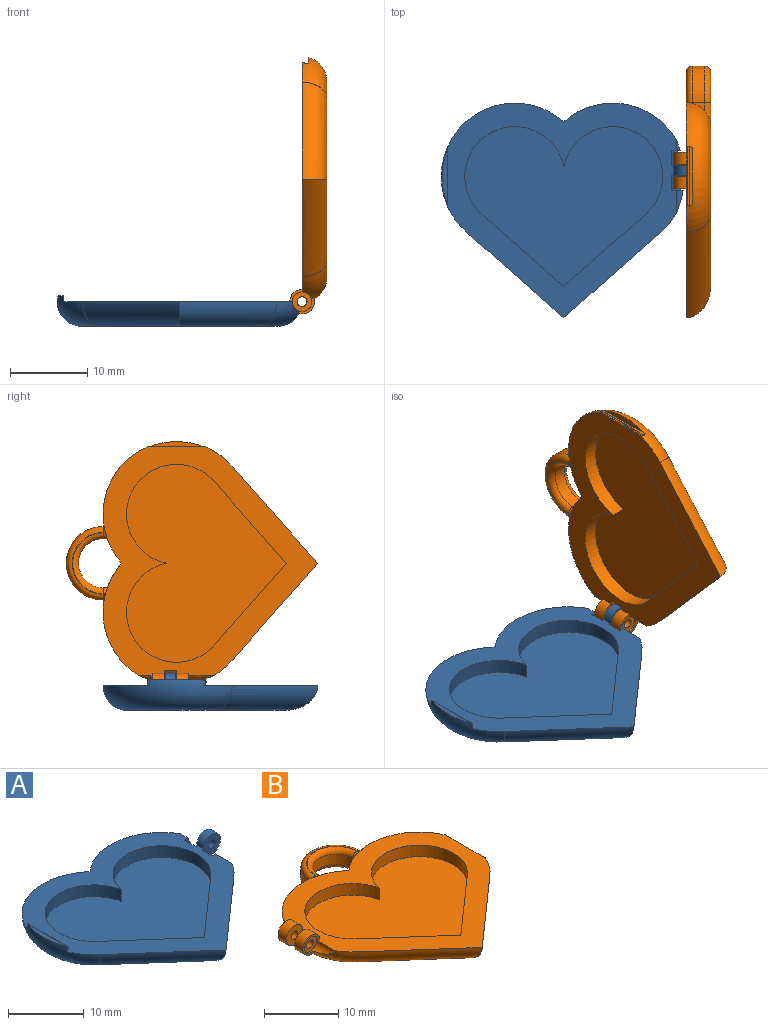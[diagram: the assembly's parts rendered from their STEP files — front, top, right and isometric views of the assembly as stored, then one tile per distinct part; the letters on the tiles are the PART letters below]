
ASSEMBLY  parts=2 mates=1
PART A: 31 faces, bbox 34.1x28.6x5.4 mm
  f0: torus R=6.35mm, axis (0,0,1), area 124.9mm2, adj f1,f2,f6,f7,f9,f20,f21,f22
  f1: cylinder r=1.27mm len=3.03mm, axis (0,1,0), area 2.4mm2, adj f0,f2,f27
  f2: plane 29.67x27.83mm, normal (0,0,1), area 243mm2, adj f0,f1,f4,f5,f6,f7,f8,f11
  f3: cylinder r=0.64mm len=1.27mm, axis (0,-1,0), area 5.1mm2, adj f22,f25
  f4: cylinder r=3.17mm len=14.69mm, axis (0.75,0.66,0), area 76.6mm2, adj f2,f5,f7,f9
  f5: cylinder r=3.17mm len=14.69mm, axis (0.75,-0.66,0), area 76.6mm2, adj f2,f4,f8,f9
  f6: torus R=6.35mm, axis (0,0,1), area 144.4mm2, adj f0,f2,f8,f9,f10,f11,f12,f28
  f7: bspline ~3.88x2.4mm, area 0.1mm2, adj f0,f2,f4
  f8: bspline ~3.36x2.4mm, area 0.1mm2, adj f2,f5,f6
  f9: plane 25.4x20.42mm, normal (0,0,-1), area 339.5mm2, adj f0,f4,f5,f6
  f10: plane 7.09x0.69mm, normal (0,0,1), area 3.3mm2, adj f6,f29
  f11: plane 7.63x0.36mm, normal (1,0,0), area 2.5mm2, adj f2,f6,f28
  f12: plane 7.6x0.11mm, normal (1,0,0), area 0.8mm2, adj f6,f29,f30
  f13: cylinder r=6.48mm len=12.83mm, axis (0,0,1), area 46.9mm2, adj f2,f14,f18,f19
  f14: cylinder r=6.48mm len=12.83mm, axis (0,0,1), area 46.9mm2, adj f2,f13,f15,f19
  f15: plane 1.91x0.04mm, normal (-0.66,0.75,0), area 0.1mm2, adj f2,f14,f16,f19
  f16: plane 10.55x9.3mm, normal (-0.66,0.75,0), area 26.8mm2, adj f2,f15,f17,f19
  f17: plane 10.55x9.3mm, normal (0.66,0.75,0), area 26.8mm2, adj f2,f16,f18,f19
  f18: plane 1.91x0.04mm, normal (0.66,0.75,0), area 0.1mm2, adj f2,f13,f17,f19
  f19: plane 25.65x20.71mm, normal (0,0,1), area 349.4mm2, adj f13,f14,f15,f16,f17,f18
  f20: cylinder r=1.59mm len=3.18mm, axis (0,-1,0), area 10.1mm2, adj f0,f2,f22,f25
  f21: cylinder r=1.91mm len=1.91mm, axis (0,1,0), area 4.5mm2, adj f0,f2,f25,f27
  f22: plane 3.49x3.38mm, normal (0,1,0), area 7.3mm2, adj f0,f2,f3,f20,f23
  f23: cylinder r=1.91mm len=1.91mm, axis (0,-1,0), area 4mm2, adj f0,f2,f22,f26
  f24: cylinder r=1.27mm len=1.44mm, axis (0,-1,0), area 0.8mm2, adj f0,f2,f26
  f25: plane 3.49x3.41mm, normal (0,-1,0), area 7.4mm2, adj f0,f2,f3,f20,f21
  f26: plane 1.59x1.16mm, normal (0,-1,0), area 1mm2, adj f0,f2,f23,f24
  f27: plane 1.77x1.53mm, normal (0,1,0), area 1.2mm2, adj f0,f1,f2,f21
  f28: cylinder r=0.06mm len=7.54mm, axis (0,1,0), area 0.2mm2, adj f6,f11,f30
  f29: cylinder r=0.06mm len=7.48mm, axis (0,-1,0), area 0.7mm2, adj f6,f10,f12
  f30: cylinder r=0.64mm len=7.59mm, axis (0,1,0), area 2.1mm2, adj f6,f12,f28
PART B: 53 faces, bbox 34.2x33.1x5.5 mm
  f0: torus R=6.35mm, axis (0,0,1), area 104mm2, adj f1,f2,f11,f12,f14,f24,f30,f49
  f1: plane 7.62x0.18mm, normal (1,0,0), area 1.3mm2, adj f0,f2,f52
  f2: plane 31.83x29.67mm, normal (0,0,1), area 244.7mm2, adj f0,f1,f4,f6,f7,f8,f9,f10
  f3: cylinder r=0.64mm len=1.33mm, axis (0,1,0), area 5.3mm2, adj f43,f47
  f4: torus R=6.35mm, axis (0,0,1), area 97.8mm2, adj f2,f10,f12,f16,f22,f28,f38,f39
  f5: cylinder r=0.64mm len=1.33mm, axis (0,1,0), area 5.3mm2, adj f40,f45
  f6: torus R=6.35mm, axis (0,0,1), area 21.2mm2, adj f2,f7,f12,f17,f19,f25
  f7: torus R=6.35mm, axis (0,0,1), area 21.2mm2, adj f2,f6,f12,f13,f21,f27
  f8: cylinder r=3.17mm len=14.69mm, axis (-0.75,0.66,0), area 78.5mm2, adj f2,f9,f10,f12
  f9: cylinder r=3.17mm len=14.69mm, axis (-0.75,-0.66,0), area 78.5mm2, adj f2,f8,f11,f12
  f10: bspline ~3.88x2.4mm, area 0.1mm2, adj f2,f4,f8
  f11: bspline ~3.36x2.4mm, area 0.1mm2, adj f0,f2,f9
  f12: plane 27.59x25.4mm, normal (0,0,-1), area 340.8mm2, adj f0,f4,f6,f7,f8,f9,f19,f20
  f13: plane 1.86x1.77mm, normal (-1,0,0), area 1.7mm2, adj f7,f18,f21,f27
  f14: plane 1.65x1.26mm, normal (1,0,0), area 1mm2, adj f0,f15,f24,f30
  f15: cylinder r=4.76mm len=9.53mm, axis (0,0,-1), area 24.7mm2, adj f14,f16,f23,f29
  f16: plane 1.71x1.32mm, normal (-1,0,0), area 1mm2, adj f4,f15,f22,f28
  f17: plane 1.86x1.77mm, normal (1,0,0), area 1.7mm2, adj f6,f18,f19,f25
  f18: cylinder r=3.17mm len=6.35mm, axis (0,0,-1), area 16.5mm2, adj f13,f17,f20,f26
  f19: cylinder r=0.76mm len=3.65mm, axis (0,1,0), area 3.2mm2, adj f6,f12,f17,f20
  f20: torus R=3.94mm, axis (0,0,1), area 13mm2, adj f12,f18,f19,f21
  f21: cylinder r=0.76mm len=3.65mm, axis (0,-1,0), area 3.2mm2, adj f7,f12,f13,f20
  f22: cylinder r=0.76mm len=3.63mm, axis (0,-1,0), area 2.9mm2, adj f4,f12,f16,f23
  f23: torus R=4mm, axis (0,0,1), area 16.9mm2, adj f12,f15,f22,f24
  f24: cylinder r=0.76mm len=3.62mm, axis (0,1,0), area 2.9mm2, adj f0,f12,f14,f23
  f25: cylinder r=0.76mm len=0.76mm, axis (0,-1,0), area 0.6mm2, adj f2,f6,f17,f26
  f26: torus R=3.94mm, axis (0,0,1), area 13mm2, adj f2,f18,f25,f27
  f27: cylinder r=0.76mm len=0.76mm, axis (0,1,0), area 0.6mm2, adj f2,f7,f13,f26
  f28: cylinder r=0.76mm len=0.76mm, axis (0,1,0), area 0.3mm2, adj f2,f4,f16,f29
  f29: torus R=4mm, axis (0,0,1), area 16.9mm2, adj f2,f15,f28,f30
  f30: cylinder r=0.76mm len=0.76mm, axis (0,-1,0), area 0.3mm2, adj f0,f2,f14,f29
  f31: plane 1.91x0.04mm, normal (-0.66,0.75,0), area 0.1mm2, adj f2,f32,f36,f37
  f32: cylinder r=6.48mm len=12.83mm, axis (0,0,1), area 46.9mm2, adj f2,f31,f33,f37
  f33: cylinder r=6.48mm len=12.83mm, axis (0,0,1), area 46.9mm2, adj f2,f32,f34,f37
  f34: plane 1.91x0.04mm, normal (0.66,0.75,0), area 0.1mm2, adj f2,f33,f35,f37
  f35: plane 10.55x9.3mm, normal (0.66,0.75,0), area 26.8mm2, adj f2,f34,f36,f37
  f36: plane 10.55x9.3mm, normal (-0.66,0.75,0), area 26.8mm2, adj f2,f31,f35,f37
  f37: plane 25.65x20.71mm, normal (0,0,1), area 349.4mm2, adj f31,f32,f33,f34,f35,f36
  f38: cylinder r=1.59mm len=3.18mm, axis (0,1,0), area 12.6mm2, adj f2,f4,f39,f40
  f39: plane 3.18x3.18mm, normal (0,-1,0), area 2.3mm2, adj f2,f4,f38,f44
  f40: plane 3.49x3.41mm, normal (0,1,0), area 7.4mm2, adj f2,f4,f5,f38,f48
  f41: cylinder r=1.59mm len=3.18mm, axis (0,-1,0), area 13mm2, adj f2,f4,f42,f43
  f42: plane 3.18x3.18mm, normal (0,1,0), area 2.4mm2, adj f2,f4,f41,f46
  f43: plane 3.49x3.37mm, normal (0,-1,0), area 7.3mm2, adj f2,f3,f4,f41,f48
  f44: cylinder r=1.27mm len=3.44mm, axis (0,1,0), area 5.6mm2, adj f2,f4,f39,f45
  f45: plane 2.54x2.54mm, normal (0,-1,0), area 3.8mm2, adj f5,f44
  f46: cylinder r=1.27mm len=2.54mm, axis (0,-1,0), area 3.3mm2, adj f2,f4,f42,f47
  f47: plane 2.54x2.54mm, normal (0,1,0), area 3.8mm2, adj f3,f46
  f48: cylinder r=1.91mm len=1.81mm, axis (0,1,0), area 3.7mm2, adj f2,f4,f40,f43
  f49: plane 7.4x0.76mm, normal (0,0,1), area 3.8mm2, adj f0,f50
  f50: plane 7.76x0.36mm, normal (1,0,0), area 2.5mm2, adj f0,f49,f51
  f51: cylinder r=0.06mm len=7.74mm, axis (0,-1,0), area 0.2mm2, adj f0,f50,f52
  f52: cylinder r=0.64mm len=7.73mm, axis (0,-1,0), area 2.1mm2, adj f0,f1,f51
PLACE A t=(0.66,4.26,5.27)mm
PLACE B rot(axis=(0,-1,0),90deg) t=(19.71,4.26,24.33)mm
MATE revolute B.f3 <-> A.f1  axis (0,1,0) through (16.52,5.05,8.46)mm
